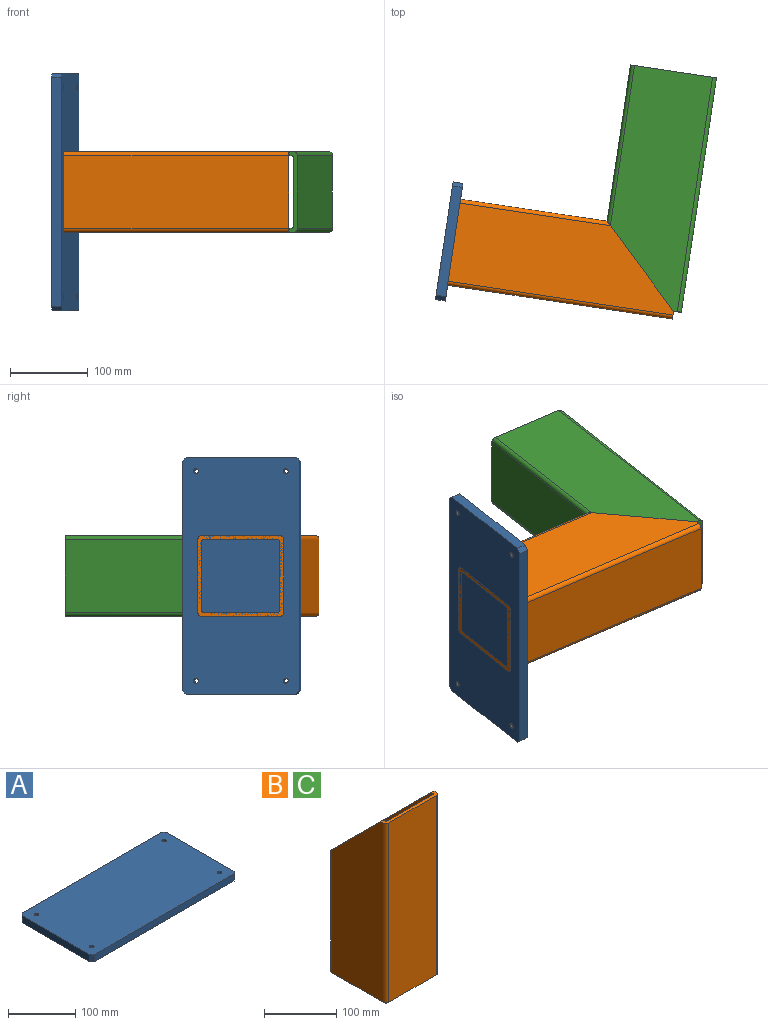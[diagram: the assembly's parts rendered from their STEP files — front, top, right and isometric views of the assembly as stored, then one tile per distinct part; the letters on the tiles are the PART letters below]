
ASSEMBLY  parts=3 mates=2
PART A: 14 faces, bbox 304.8x152.4x12.7 mm
  f0: plane 142.24x12.7mm, normal (-1,0,0), area 1806.4mm2, adj f4,f5,f6,f7
  f1: plane 294.64x12.7mm, normal (0,-1,0), area 3741.9mm2, adj f4,f5,f6,f9
  f2: plane 142.24x12.7mm, normal (1,0,0), area 1806.4mm2, adj f4,f5,f8,f9
  f3: plane 294.64x12.7mm, normal (0,1,0), area 3741.9mm2, adj f4,f5,f7,f8
  f4: plane 304.8x152.4mm, normal (0,0,1), area 46263.1mm2, adj f0,f1,f2,f3,f6,f7,f8,f9
  f5: plane 304.8x152.4mm, normal (0,0,-1), area 46263.1mm2, adj f0,f1,f2,f3,f6,f7,f8,f9
  f6: plane 12.7x5.08mm, normal (-0.71,-0.71,0), area 91.2mm2, adj f0,f1,f4,f5
  f7: plane 12.7x5.08mm, normal (-0.71,0.71,0), area 91.2mm2, adj f0,f3,f4,f5
  f8: plane 12.7x5.08mm, normal (0.71,0.71,0), area 91.2mm2, adj f2,f3,f4,f5
  f9: plane 12.7x5.08mm, normal (0.71,-0.71,0), area 91.2mm2, adj f1,f2,f4,f5
  f10: cylinder r=3.3mm len=12.7mm, axis (0,0,-1), area 263.3mm2, adj f4,f5
  f11: cylinder r=3.3mm len=12.7mm, axis (0,0,-1), area 263.3mm2, adj f4,f5
  f12: cylinder r=3.3mm len=12.7mm, axis (0,0,-1), area 263.3mm2, adj f4,f5
  f13: cylinder r=3.3mm len=12.7mm, axis (0,0,-1), area 263.3mm2, adj f4,f5
PART B: 19 faces, bbox 104x111.7x304.8 mm
  f0: cylinder r=2.54mm len=304.8mm, axis (0,0,-1), area 1216.1mm2, adj f1,f15,f16,f17
  f1: plane 304.8x88.73mm, normal (0,1,0), area 27044.4mm2, adj f0,f2,f16,f17
  f2: cylinder r=2.54mm len=304.8mm, axis (0,0,-1), area 1216.1mm2, adj f1,f3,f16,f17
  f3: plane 304.8x96.49mm, normal (1,0,0), area 24994.4mm2, adj f2,f4,f16,f17,f18
  f4: cylinder r=2.54mm len=210.82mm, axis (0,0,-1), area 834.7mm2, adj f3,f5,f17,f18
  f5: plane 208.28x88.73mm, normal (0,-1,0), area 18480.3mm2, adj f4,f6,f17,f18
  f6: cylinder r=2.54mm len=210.82mm, axis (0,0,-1), area 834.7mm2, adj f5,f15,f17,f18
  f7: plane 304.8x93.81mm, normal (0,-1,0), area 28592.8mm2, adj f8,f14,f16,f17
  f8: cylinder r=5.08mm len=304.8mm, axis (0,0,-1), area 2432.2mm2, adj f7,f9,f16,f17
  f9: plane 304.8x101.57mm, normal (1,0,0), area 26300.9mm2, adj f8,f10,f16,f17,f18
  f10: cylinder r=5.08mm len=208.28mm, axis (0,0,-1), area 1636.2mm2, adj f9,f11,f17,f18
  f11: plane 203.2x93.81mm, normal (0,1,0), area 19061.9mm2, adj f10,f12,f17,f18
  f12: cylinder r=5.08mm len=208.28mm, axis (0,0,-1), area 1636.2mm2, adj f11,f13,f17,f18
  f13: plane 304.8x101.57mm, normal (-1,0,0), area 26300.9mm2, adj f12,f14,f16,f17,f18
  f14: cylinder r=5.08mm len=304.8mm, axis (0,0,-1), area 2432.2mm2, adj f7,f13,f16,f17
  f15: plane 304.8x96.49mm, normal (-1,0,0), area 24994.4mm2, adj f0,f6,f16,f17,f18
  f16: plane 103.97x10.13mm, normal (0,0,1), area 571.2mm2, adj f0,f1,f2,f3,f7,f8,f9,f13
  f17: plane 111.73x103.97mm, normal (0,0,-1), area 2071.7mm2, adj f0,f1,f2,f3,f4,f5,f6,f7
  f18: plane 103.97x101.6mm, normal (0,0.71,0.71), area 2122mm2, adj f3,f4,f5,f6,f9,f10,f11,f12
PART C: same geometry as B
PLACE A rot(axis=(-0.71,0.05,0.71),174deg) t=(-374.01,-160.85,144.37)mm
PLACE B rot(axis=(0.07,0.99,-0.07),90.3deg) t=(-386.03,-155.37,147.55)mm
PLACE C rot(axis=(0.55,-0.63,0.55),115.2deg) t=(-97.09,58.05,149.92)mm
MATE fastened C.f18 <-> B.f18  axis (-0.8,-0.59,0) through (-147.49,-176.01,148.73)mm
MATE fastened A.f4 <-> B.f17  axis (-0.99,0.15,0) through (-386.78,-160.38,148.73)mm
